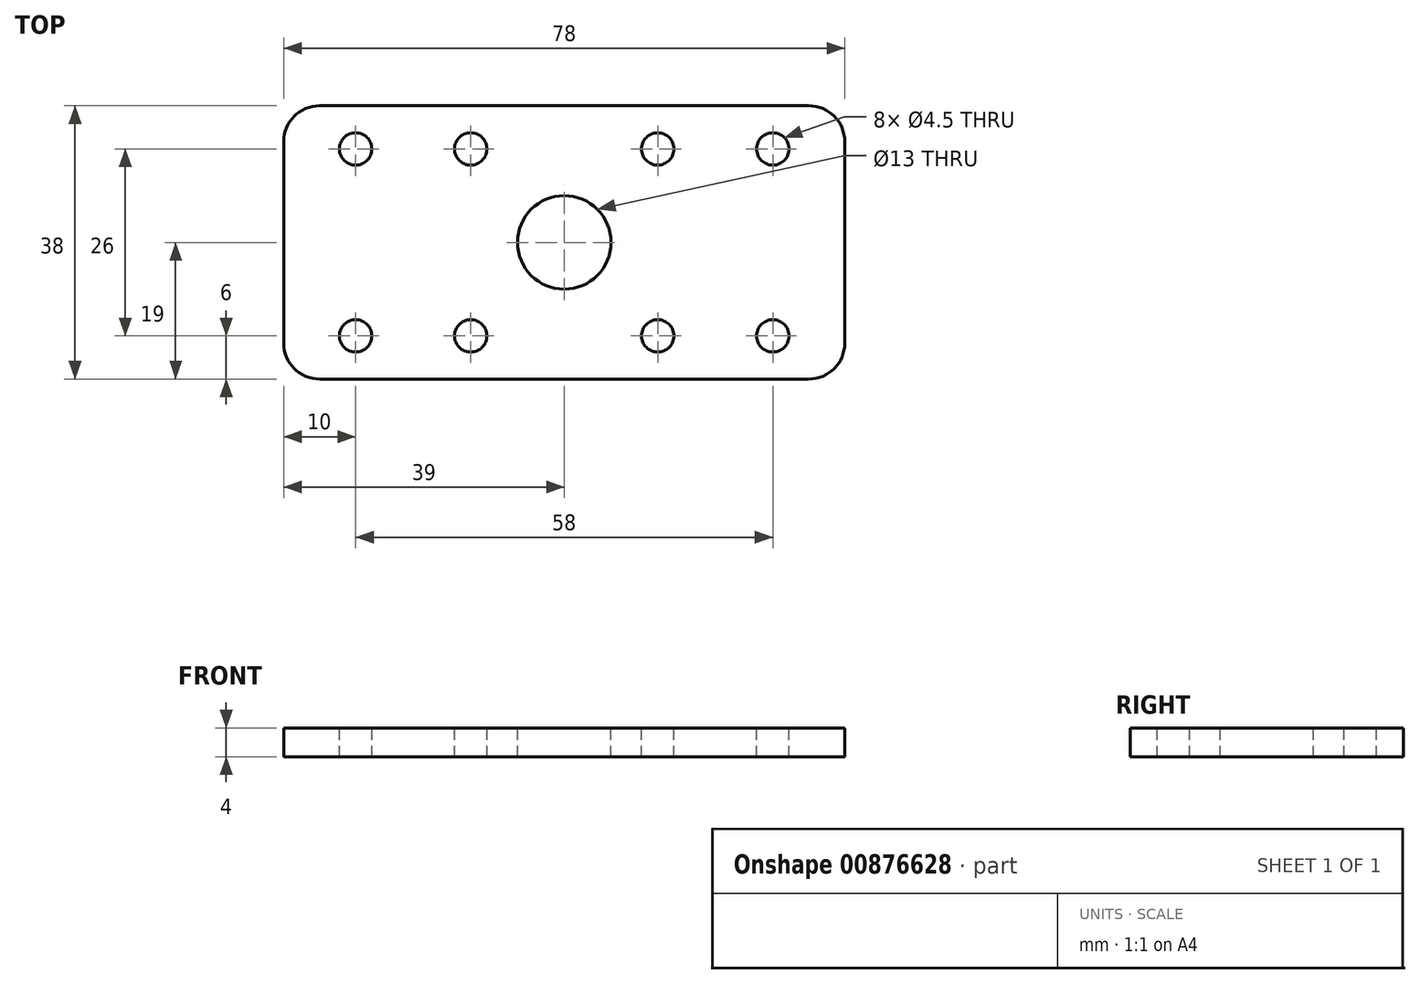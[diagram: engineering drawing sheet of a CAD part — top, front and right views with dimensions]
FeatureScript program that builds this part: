
annotation { "Feature Type Name" : "Feature", "Feature Type Description" : "" }
export const myFeature = defineFeature(function(context is Context, id is Id, definition is map)
    precondition{}
    {
        {
            var Q0;
            Q0=qCreatedBy(makeId("Top.planeOp"),FACE);
            var sketch = newSketch(context, id + "F0", { "sketchPlane" : qUnion([Q0])});
            skLineSegment(sketch, "E0.bottom", {"start": v(39, 19) * mm, "end": v(-39, 19) * mm});
            skLineSegment(sketch, "E0.top", {"start": v(39, -19) * mm, "end": v(-39, -19) * mm});
            skLineSegment(sketch, "E0.left", {"start": v(39, 19) * mm, "end": v(39, -19) * mm});
            skLineSegment(sketch, "E0.right", {"start": v(-39, 19) * mm, "end": v(-39, -19) * mm});
            skPoint(sketch, "E0.middle", {"position": v(0, 0) * mm});
            skLineSegment(sketch, "E1.0", {"start": v(39, 13) * mm, "end": v(-39, 13) * mm, "construction": true});
            skLineSegment(sketch, "E2.0", {"start": v(-13, 19) * mm, "end": v(-13, -19) * mm, "construction": true});
            skLineSegment(sketch, "E3.0", {"start": v(13, 19) * mm, "end": v(13, -19) * mm, "construction": true});
            skLineSegment(sketch, "E4.0", {"start": v(39, -13) * mm, "end": v(-39, -13) * mm, "construction": true});
            skCircle(sketch, "E5", {"center": v(-13, 13) * mm, "radius": 2.25 * mm});
            skLineSegment(sketch, "E6", {"start": v(-39, 0) * mm, "end": v(39, 0) * mm, "construction": true});
            skLineSegment(sketch, "E7", {"start": v(0, 19) * mm, "end": v(0, -19) * mm, "construction": true});
            skCircle(sketch, "E8.MirrorC", {"center": v(13, 13) * mm, "radius": 2.25 * mm});
            skCircle(sketch, "E9.MirrorC", {"center": v(13, -13) * mm, "radius": 2.25 * mm});
            skCircle(sketch, "E10.MirrorC", {"center": v(-13, -13) * mm, "radius": 2.25 * mm});
            skCircle(sketch, "E11", {"center": v(0, 0) * mm, "radius": 6.5 * mm});
            skLineSegment(sketch, "E12.0", {"start": v(-29, 19) * mm, "end": v(-29, -19) * mm, "construction": true});
            skLineSegment(sketch, "E13.0", {"start": v(29, 19) * mm, "end": v(29, -19) * mm, "construction": true});
            skCircle(sketch, "E14", {"center": v(-29, 13) * mm, "radius": 2.25 * mm});
            skCircle(sketch, "E15.MirrorC", {"center": v(29, 13) * mm, "radius": 2.25 * mm});
            skCircle(sketch, "E16.MirrorC", {"center": v(29, -13) * mm, "radius": 2.25 * mm});
            skCircle(sketch, "E17.MirrorC", {"center": v(-29, -13) * mm, "radius": 2.25 * mm});
            skSolve(sketch);
        }
        {
            var Q0;
            Q0=makeQuery(id+"F0.imprint","IMPRINT",FACE,{"disambiguationData":[TD([[makeQuery(id+"F0.imprint","IMPRINT",EDGE,{"derivedFrom":sQuery(id+"F0.wireOp",EDGE,"E0.bottom")}),1.0]])]});
            var Q1;
            Q1=makeQuery(id+"F0.imprint","IMPRINT",FACE,{"disambiguationData":[TD([[makeQuery(id+"F0.imprint","IMPRINT",EDGE,{"derivedFrom":sQuery(id+"F0.wireOp",EDGE,"HWjcr97h-bGiZ-oV4i-kZyB-UvR0nVrvKp9y")}),1.0]])]});
            extrude(context, id + "F1", {"entities" : qUnion([Q0, Q1]), "oppositeDirection" : true, "depth" : 4 * mm, "offsetDistance" : 25 * mm});
        }
        {
            var Q0;
            Q0=makeQuery(id+"F1.opExtrude","SWEPT_EDGE",EDGE,{"disambiguationData":[OSD([sQuery(id+"F0.wireOp",EDGE,"E0.top"),sQuery(id+"F0.wireOp",EDGE,"E0.right")])]});
            var Q1;
            Q1=makeQuery(id+"F1.opExtrude","SWEPT_EDGE",EDGE,{"disambiguationData":[OSD([sQuery(id+"F0.wireOp",EDGE,"E0.top"),sQuery(id+"F0.wireOp",EDGE,"E0.left")])]});
            var Q2;
            Q2=makeQuery(id+"F1.opExtrude","SWEPT_EDGE",EDGE,{"disambiguationData":[OSD([sQuery(id+"F0.wireOp",EDGE,"E0.bottom"),sQuery(id+"F0.wireOp",EDGE,"E0.left")])]});
            var Q3;
            Q3=makeQuery(id+"F1.opExtrude","SWEPT_EDGE",EDGE,{"disambiguationData":[OSD([sQuery(id+"F0.wireOp",EDGE,"E0.bottom"),sQuery(id+"F0.wireOp",EDGE,"E0.right")])]});
            fillet(context, id + "F2", {"entities" : qUnion([Q0, Q1, Q2, Q3]), "radius" : 5 * mm, "tangentPropagation" : true, "allowEdgeOverflow" : false});
        }
    });
